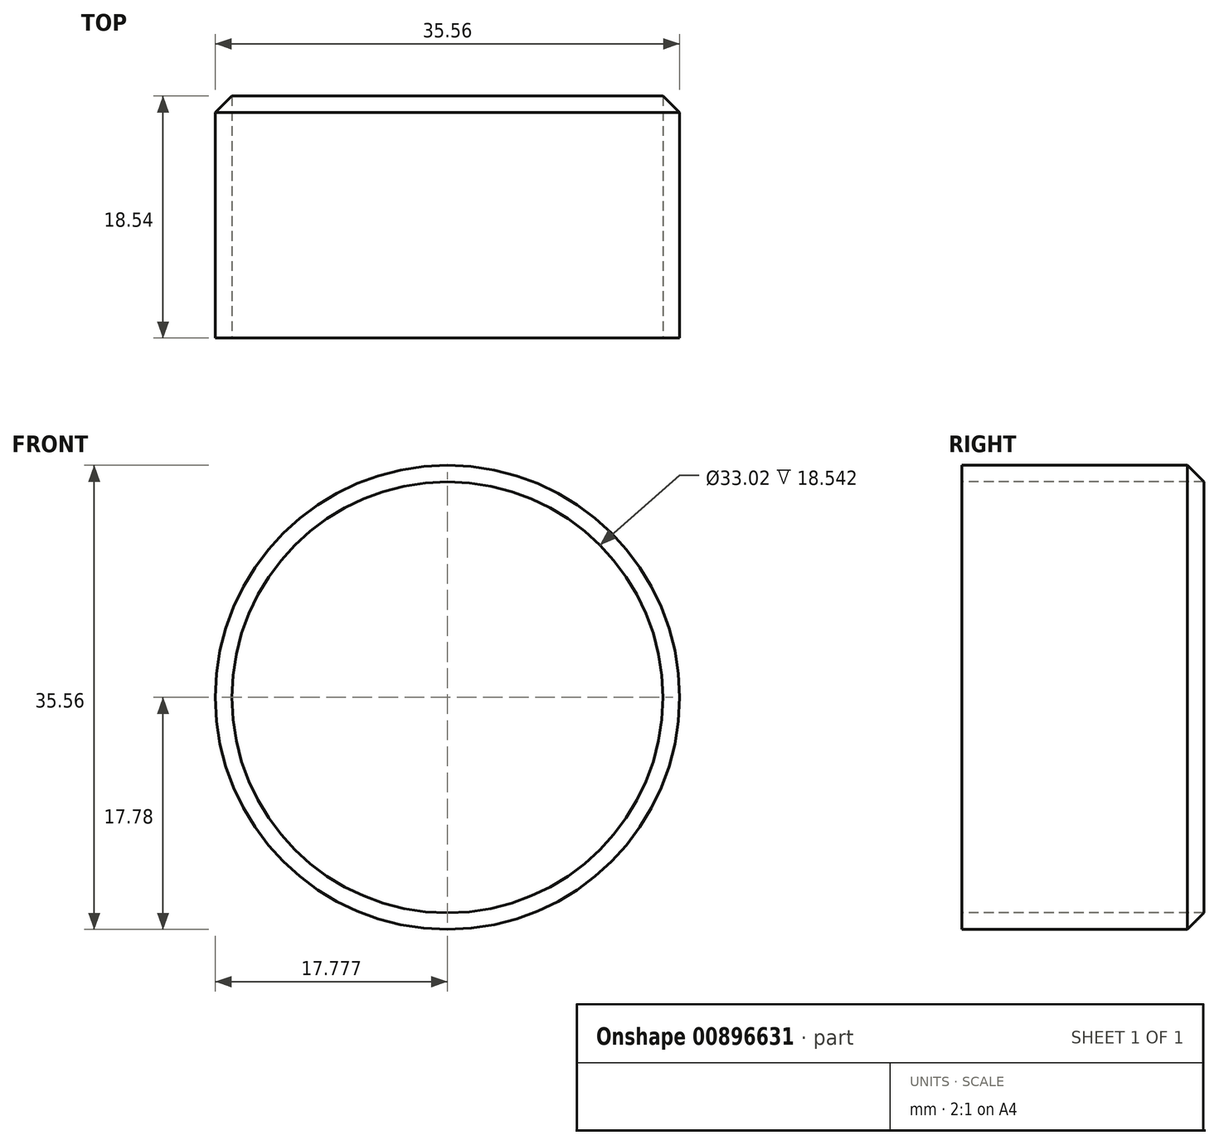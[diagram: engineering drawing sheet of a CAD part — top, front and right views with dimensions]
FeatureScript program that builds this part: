
annotation { "Feature Type Name" : "Feature", "Feature Type Description" : "" }
export const myFeature = defineFeature(function(context is Context, id is Id, definition is map)
    precondition{}
    {
        {
            var Q0;
            Q0=qCreatedBy(makeId("Front.planeOp"),FACE);
            var sketch = newSketch(context, id + "F0", { "sketchPlane" : qUnion([Q0])});
            skCircle(sketch, "E0", {"center": v(-65.97, 0) * mm, "radius": 17.78 * mm});
            skCircle(sketch, "E1", {"center": v(-65.97, 0) * mm, "radius": 16.51 * mm});
            skSolve(sketch);
        }
        {
            var Q0;
            Q0=makeQuery(id+"F0.imprint","IMPRINT",FACE,{"disambiguationData":[TD([[makeQuery(id+"F0.imprint","IMPRINT",EDGE,{"derivedFrom":sQuery(id+"F0.wireOp",EDGE,"E0")}),1.0]])]});
            extrude(context, id + "F1", {"entities" : qUnion([Q0]), "oppositeDirection" : true, "depth" : 19.8 * mm, "offsetDistance" : 25.4 * mm});
        }
        {
            var Q0;
            Q0=makeQuery(id+"F1.opExtrude","CAP_EDGE",EDGE,{"disambiguationData":[OSD([sQuery(id+"F0.wireOp",EDGE,"E0")])],"isStart":false});
            chamfer(context, id + "F2", {"entities" : qUnion([Q0]), "width" : 2.54 * mm, "tangentPropagation" : true});
        }
    });
